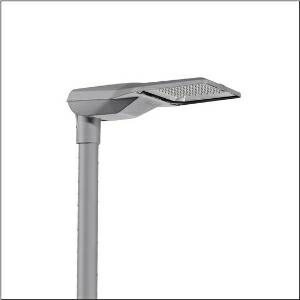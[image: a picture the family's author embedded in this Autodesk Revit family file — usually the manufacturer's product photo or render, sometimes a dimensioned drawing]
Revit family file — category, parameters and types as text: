
# Revit family: streetlight_sl_21_midi___st0_8a_5xe7c43a08nb_588f
name_source: partatom
category: Lighting Fixtures
units: mm (PartAtom-declared; Revit-internal decimal feet)

## family parameters
Cut with Voids When Loaded = No
Host = Face
Light Source = No
Part Type = Normal
Room Calculation Point = No
Round Connector Dimension = Use Diameter
Shared = No

## types (1)
- --- (1 x LED, 23710 lm, 151.2 W, 4000K)
    Apparent Load = 151 VA
    CIE Flux Codes = 41 75 97 100 100
    Color Rendering = 70
    Color Temperature = 4000K
    Default Elevation = 1800 mm
    Description = Streetlight SL 21 midi, mast luminaire, primary light control with lens, of PMMA, primary optical cover: cover, of toughened safety glass, transparent, light distribution: ST0.8a, light emission: direct distribution, primary light characteristic: asymmetric, installation type: post-top, side-entry, LED, 3G 1.5mm², High Power LED, rated luminous flux: 23.710lm, luminous efficacy: 157lm/W, light colour: 740, colour temperature: 4000K, control gear: Easy, control: overheat protection, constant luminous flux control, time-dependent luminous flux control, flexible luminous flux parameterisation, mains connection: 220..240V, AC, 50/60Hz, connection cable pre-assembled, cable length: 12,5m, wiring characteristics: H07RN-F, start of lifetime: 151W, end of service life: 157W, reduction: 71W, luminaire housing, of diecast aluminium, powder-coated, Siteco® metallic grey (DB 702S), corrosivity category C5 mid according to DIN EN ISO 12944, please order mast flange separately, inclination adjustable: 0°, 5°, 10°, 15°, sealing non-destructively replaceable, multi-level sealing system, length: 644mm, width: 335mm, height: 110mm, mast flange for spigot size: 42mm (side-entry): 5XC10008XM4, 60/48mm (side-entry/post-top): 5XC10108XM2, 76/60mm (side-entry/post-top): 5XC10108XM1, mounting height: 4..8m, protection rating (complete): IP66, insulation class (complete): insulation class II (safety insulation), certification: CE, ENEC, ENEC+, VDE, impact resistance: IK10, permissible operating ambient temperature for outdoor applications: -40..+50°C, standard-compliant lighting for roads and squares, packaging unit: 1 piece

Light Distribution: ST0.8a
    Height = 111 mm
    Lamp = 1 x LED
    Lamp Light Flux = 23710 lm
    Lamp Power = 151.2 W
    Lamp count = 1
    Length = 644 mm
    Luminous efficacy = 157 lm/W
    Manufacturer = Siteco
    ModVariant = No
    Model = 5XE7C43A08NB
    Number of Poles = 1
    OnlyDefault = Yes
    Power Factor = 1
    Product Name = Streetlight SL 21 midi | ST0.8a
    Product group = mast luminaire | pylon top
    ProductGroupID = 6100
    Protection Class = Protection class II
    Protection Degree = IP 66
    RLX_Detail_Level = 1
    RLX_Emergency_Light_Flux = 0 lm
    RLX_Emergency_Type = 0
    RLX_Emergency_Type_DB = No
    RlxData = <blob elided: 26729 chars, md5=318b5dca>
    Socket = socket
    Standby Power = 0 W
    System Light Flux = 23710 lm
    System Power = 151 W
    Type Comments = factory setting: luminous flux: 100 % | Output Level: 100 % | 802 mA
    Type Image = l_1004298.jpg
    URL = http://relux.com
    VarID = @adj_189919
    Voltage = 0 V
    Weight = 0.00 kg
    Width = 336 mm

## geometry (parser evidence)
native form markers: Blend x4, Sweep x11
no freeform markers — native parametric forms only
